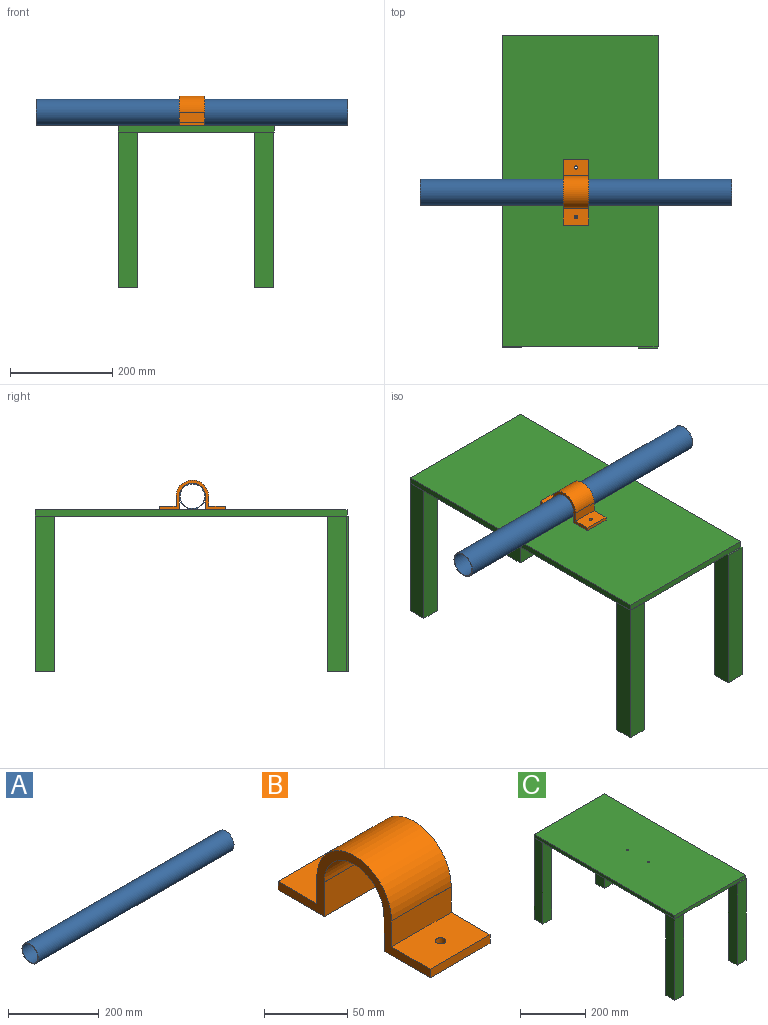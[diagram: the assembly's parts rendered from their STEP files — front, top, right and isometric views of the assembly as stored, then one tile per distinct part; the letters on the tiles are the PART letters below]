
ASSEMBLY  parts=3 mates=2
PART A: 4 faces, bbox 609.6x50.8x50.8 mm
  f0: cylinder r=23.81mm len=609.6mm, axis (1,0,0), area 91207.3mm2, adj f2,f3
  f1: cylinder r=25.4mm len=609.6mm, axis (1,0,0), area 97287.8mm2, adj f2,f3
  f2: plane 50.8x50.8mm, normal (-1,0,0), area 245.4mm2, adj f0,f1
  f3: plane 50.8x50.8mm, normal (1,0,0), area 245.4mm2, adj f0,f1
PART B: 19 faces, bbox 50.8x129.5x57.6 mm
  f0: plane 50.8x39.37mm, normal (0,0,-1), area 1968.3mm2, adj f1,f14,f15,f16,f17
  f1: plane 50.8x25.24mm, normal (0,1,0), area 1282.4mm2, adj f0,f2,f15,f16
  f2: plane 50.8x0.05mm, normal (0,0.72,-0.7), area 3.3mm2, adj f1,f3,f15,f16
  f3: cylinder r=25.4mm len=50.8mm, axis (-1,0,0), area 4108mm2, adj f2,f4,f15,f16
  f4: plane 50.8x0.03mm, normal (0,0,1), area 1.8mm2, adj f3,f5,f15,f16
  f5: plane 50.8x25.4mm, normal (0,-1,0), area 1290.3mm2, adj f4,f6,f15,f16
  f6: plane 50.8x39.37mm, normal (0,0,-1), area 1968.3mm2, adj f5,f7,f15,f16,f18
  f7: plane 50.8x6.35mm, normal (0,1,0), area 322.6mm2, adj f6,f8,f15,f16
  f8: plane 50.8x33.02mm, normal (0,0,1), area 1645.7mm2, adj f7,f9,f15,f16,f18
  f9: plane 50.8x17.96mm, normal (0,1,0), area 912.2mm2, adj f8,f10,f15,f16
  f10: cylinder r=31.75mm len=63.5mm, axis (-1,0,0), area 5171.5mm2, adj f9,f11,f15,f16
  f11: plane 50.8x0.04mm, normal (0,0,1), area 2.2mm2, adj f10,f12,f15,f16
  f12: plane 50.8x19.05mm, normal (0,-1,0), area 967.7mm2, adj f11,f13,f15,f16
  f13: plane 50.8x33.02mm, normal (0,0,1), area 1645.7mm2, adj f12,f14,f15,f16,f17
  f14: plane 50.8x6.35mm, normal (0,-1,0), area 322.6mm2, adj f0,f13,f15,f16
  f15: plane 129.54x57.63mm, normal (1,0,0), area 1318.1mm2, adj f0,f1,f2,f3,f4,f5,f6,f7
  f16: plane 129.54x57.63mm, normal (-1,0,0), area 1318.1mm2, adj f0,f1,f2,f3,f4,f5,f6,f7
  f17: cylinder r=3.17mm len=6.35mm, axis (0,0,-1), area 126.7mm2, adj f0,f13
  f18: cylinder r=3.17mm len=6.35mm, axis (0,0,-1), area 126.7mm2, adj f6,f8
PART C: 29 faces, bbox 304.8x613.2x317.5 mm
  f0: plane 609.6x304.8mm, normal (0,0,-1), area 180072.2mm2, adj f1,f2,f3,f4,f6,f7,f8,f9
  f1: plane 304.8x12.7mm, normal (0,1,0), area 3871mm2, adj f0,f2,f4,f5
  f2: plane 609.6x12.7mm, normal (-1,0,0), area 7741.9mm2, adj f0,f1,f3,f5
  f3: plane 304.8x12.7mm, normal (0,-1,0), area 3871mm2, adj f0,f2,f4,f5,f21
  f4: plane 609.6x12.7mm, normal (1,0,0), area 7741.9mm2, adj f0,f1,f3,f5
  f5: plane 609.6x304.8mm, normal (0,0,1), area 185742.7mm2, adj f1,f2,f3,f4,f27,f28
  f6: plane 304.8x38.1mm, normal (0,1,0), area 11612.9mm2, adj f0,f7,f9,f10
  f7: plane 304.8x38.1mm, normal (-1,0,0), area 11612.9mm2, adj f0,f6,f8,f10
  f8: plane 304.8x38.1mm, normal (0,-1,0), area 11612.9mm2, adj f0,f7,f9,f10
  f9: plane 304.8x38.1mm, normal (1,0,0), area 11612.9mm2, adj f0,f6,f8,f10
  f10: plane 38.1x38.1mm, normal (0,0,-1), area 1451.6mm2, adj f6,f7,f8,f9
  f11: plane 304.8x38.1mm, normal (1,0,0), area 11612.9mm2, adj f0,f12,f14,f15
  f12: plane 304.8x38.1mm, normal (0,1,0), area 11612.9mm2, adj f0,f11,f13,f15
  f13: plane 304.8x38.1mm, normal (-1,0,0), area 11612.9mm2, adj f0,f12,f14,f15
  f14: plane 304.8x38.1mm, normal (0,-1,0), area 11612.9mm2, adj f0,f11,f13,f15
  f15: plane 38.1x38.1mm, normal (0,0,-1), area 1451.6mm2, adj f11,f12,f13,f14
  f16: plane 304.8x38.1mm, normal (-1,0,0), area 11612.9mm2, adj f0,f17,f19,f20
  f17: plane 304.8x38.1mm, normal (0,-1,0), area 11612.9mm2, adj f0,f16,f18,f20
  f18: plane 304.8x38.1mm, normal (1,0,0), area 11612.9mm2, adj f0,f17,f19,f20
  f19: plane 304.8x38.1mm, normal (0,1,0), area 11612.9mm2, adj f0,f16,f18,f20
  f20: plane 38.1x38.1mm, normal (0,0,-1), area 1451.6mm2, adj f16,f17,f18,f19
  f21: plane 38.1x3.57mm, normal (0,0,1), area 135.9mm2, adj f3,f22,f23,f25
  f22: plane 304.8x38.1mm, normal (0,-1,0), area 11612.9mm2, adj f21,f23,f25,f26
  f23: plane 304.8x38.1mm, normal (1,0,0), area 11612.9mm2, adj f0,f21,f22,f24,f26
  f24: plane 304.8x38.1mm, normal (0,1,0), area 11612.9mm2, adj f0,f23,f25,f26
  f25: plane 304.8x38.1mm, normal (-1,0,0), area 11612.9mm2, adj f0,f21,f22,f24,f26
  f26: plane 38.1x38.1mm, normal (0,0,-1), area 1451.6mm2, adj f22,f23,f24,f25
  f27: cylinder r=3.17mm len=12.7mm, axis (0,0,-1), area 253.4mm2, adj f0,f5
  f28: cylinder r=3.17mm len=12.7mm, axis (0,0,-1), area 253.4mm2, adj f0,f5
PLACE A t=(-12.18,-14.72,-5.27)mm
PLACE B t=(-37.58,-4.63,-19.62)mm
PLACE C t=(-12.18,8.35,-31.6)mm
MATE fastened B.f18 <-> C.f28  axis (0,0,-1) through (-12.18,22.32,-18.9)mm
MATE fastened A.f0 <-> B.f3  axis (1,0,0) through (-12.18,-25.9,6.98)mm
